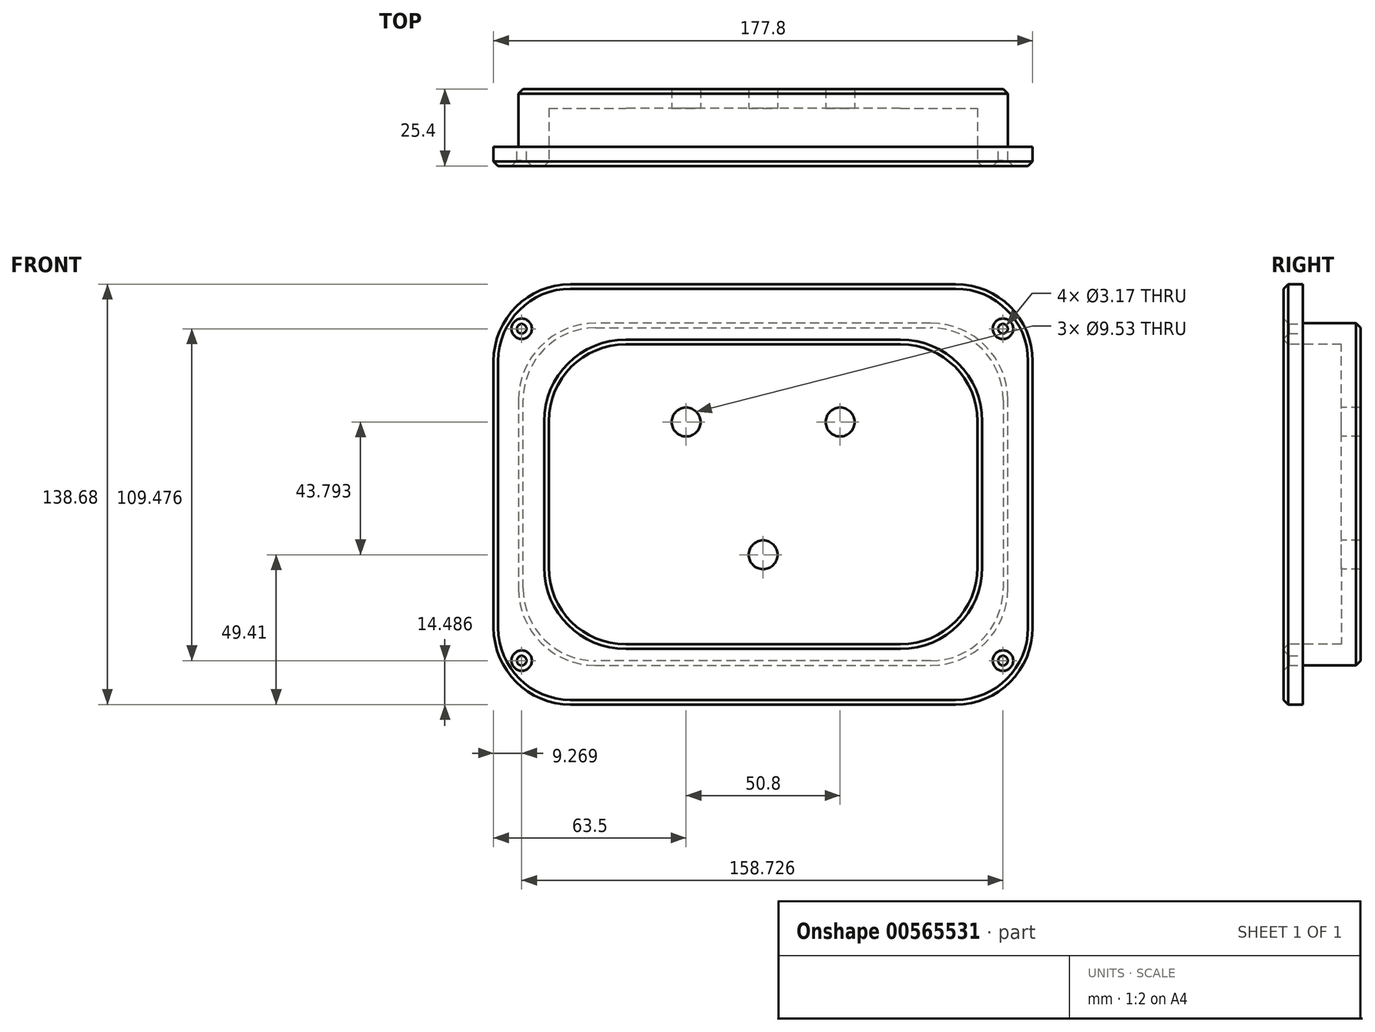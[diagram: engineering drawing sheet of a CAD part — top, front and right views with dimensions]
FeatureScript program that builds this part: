
annotation { "Feature Type Name" : "Feature", "Feature Type Description" : "" }
export const myFeature = defineFeature(function(context is Context, id is Id, definition is map)
    precondition{}
    {
        {
            var Q0;
            Q0=qCreatedBy(makeId("Front.planeOp"),FACE);
            var sketch = newSketch(context, id + "F0", { "sketchPlane" : qUnion([Q0])});
            skLineSegment(sketch, "E0.bottom", {"start": v(88.9, 69.34) * mm, "end": v(-88.9, 69.34) * mm});
            skLineSegment(sketch, "E0.top", {"start": v(88.9, -69.34) * mm, "end": v(-88.9, -69.34) * mm});
            skLineSegment(sketch, "E0.left", {"start": v(88.9, 69.34) * mm, "end": v(88.9, -69.34) * mm});
            skLineSegment(sketch, "E0.right", {"start": v(-88.9, 69.34) * mm, "end": v(-88.9, -69.34) * mm});
            skPoint(sketch, "E0.middle", {"position": v(0, 0) * mm});
            skSolve(sketch);
        }
        {
            var Q0;
            Q0=makeQuery(id+"F0.imprint","IMPRINT",FACE,{"disambiguationData":[TD([[makeQuery(id+"F0.imprint","IMPRINT",EDGE,{"derivedFrom":sQuery(id+"F0.wireOp",EDGE,"E0.bottom")}),1.0]])]});
            extrude(context, id + "F1", {"entities" : qUnion([Q0]), "depth" : 25.4 * mm, "offsetDistance" : 25.4 * mm});
        }
        {
            var Q0;
            Q0=makeQuery(id+"F1.opExtrude","CAP_FACE",FACE,{"disambiguationData":[OSD([sQuery(id+"F0.wireOp",EDGE,"E0.bottom"),sQuery(id+"F0.wireOp",EDGE,"E0.top"),sQuery(id+"F0.wireOp",EDGE,"E0.left"),sQuery(id+"F0.wireOp",EDGE,"E0.right")])],"isStart":true});
            var sketch = newSketch(context, id + "F2", { "sketchPlane" : qUnion([Q0])});
            skLineSegment(sketch, "E1.bottom", {"start": v(80.69, -56.44) * mm, "end": v(-80.69, -56.44) * mm});
            skLineSegment(sketch, "E1.top", {"start": v(80.69, 56.44) * mm, "end": v(-80.69, 56.44) * mm});
            skLineSegment(sketch, "E1.left", {"start": v(80.69, -56.44) * mm, "end": v(80.69, 56.44) * mm});
            skLineSegment(sketch, "E1.right", {"start": v(-80.69, -56.44) * mm, "end": v(-80.69, 56.44) * mm});
            skPoint(sketch, "E1.middle", {"position": v(0, 0) * mm});
            skSolve(sketch);
        }
        {
            var Q0;
            Q0=makeQuery(id+"F2.imprint","IMPRINT",FACE,{"disambiguationData":[TD([[makeQuery(id+"F2.imprint","IMPRINT",EDGE,{"derivedFrom":sQuery(id+"F2.wireOp",EDGE,"E1.bottom")}),1.0]])]});
            extrude(context, id + "F3", {"entities" : qUnion([Q0]), "operationType" : NewBodyOperationType.REMOVE, "oppositeDirection" : true, "depth" : 19.05 * mm, "offsetDistance" : 25.4 * mm});
        }
        {
            var Q0;
            Q0=makeQuery(id+"F1.opExtrude","CAP_FACE",FACE,{"disambiguationData":[OSD([sQuery(id+"F0.wireOp",EDGE,"E0.bottom"),sQuery(id+"F0.wireOp",EDGE,"E0.top"),sQuery(id+"F0.wireOp",EDGE,"E0.left"),sQuery(id+"F0.wireOp",EDGE,"E0.right")])],"isStart":false});
            var sketch = newSketch(context, id + "F4", { "sketchPlane" : qUnion([Q0])});
            skLineSegment(sketch, "E2.bottom", {"start": v(70.71, -49.5) * mm, "end": v(-70.71, -49.5) * mm});
            skLineSegment(sketch, "E2.top", {"start": v(70.71, 49.5) * mm, "end": v(-70.71, 49.5) * mm});
            skLineSegment(sketch, "E2.left", {"start": v(70.71, -49.5) * mm, "end": v(70.71, 49.5) * mm});
            skLineSegment(sketch, "E2.right", {"start": v(-70.71, -49.5) * mm, "end": v(-70.71, 49.5) * mm});
            skPoint(sketch, "E2.middle", {"position": v(0, 0) * mm});
            skSolve(sketch);
        }
        {
            var Q0;
            Q0=makeQuery(id+"F4.imprint","IMPRINT",FACE,{"disambiguationData":[TD([[makeQuery(id+"F4.imprint","IMPRINT",EDGE,{"derivedFrom":sQuery(id+"F4.wireOp",EDGE,"E2.bottom")}),-1.0]])]});
            extrude(context, id + "F5", {"entities" : qUnion([Q0]), "operationType" : NewBodyOperationType.REMOVE, "oppositeDirection" : true, "depth" : 19.05 * mm, "offsetDistance" : 25.4 * mm});
        }
        {
            var Q0;
            Q0=makeQuery(id+"F1.opExtrude","SWEPT_EDGE",EDGE,{"disambiguationData":[OSD([sQuery(id+"F0.wireOp",EDGE,"E0.bottom"),sQuery(id+"F0.wireOp",EDGE,"E0.left")])]});
            var Q1;
            Q1=makeQuery(id+"F1.opExtrude","SWEPT_EDGE",EDGE,{"disambiguationData":[OSD([sQuery(id+"F0.wireOp",EDGE,"E0.top"),sQuery(id+"F0.wireOp",EDGE,"E0.left")])]});
            var Q2;
            Q2=makeQuery(id+"F1.opExtrude","SWEPT_EDGE",EDGE,{"disambiguationData":[OSD([sQuery(id+"F0.wireOp",EDGE,"E0.top"),sQuery(id+"F0.wireOp",EDGE,"E0.right")])]});
            var Q3;
            Q3=makeQuery(id+"F1.opExtrude","SWEPT_EDGE",EDGE,{"disambiguationData":[OSD([sQuery(id+"F0.wireOp",EDGE,"E0.bottom"),sQuery(id+"F0.wireOp",EDGE,"E0.right")])]});
            var Q4;
            Q4=makeQuery(id+"F5.boolean.opBoolean","COPY",EDGE,{"derivedFrom":makeQuery(id+"F5.opExtrude","SWEPT_EDGE",EDGE,{"disambiguationData":[OSD([sQuery(id+"F4.wireOp",EDGE,"E2.top"),sQuery(id+"F4.wireOp",EDGE,"E2.right")])]})});
            var Q5;
            Q5=makeQuery(id+"F5.boolean.opBoolean","COPY",EDGE,{"derivedFrom":makeQuery(id+"F5.opExtrude","SWEPT_EDGE",EDGE,{"disambiguationData":[OSD([sQuery(id+"F4.wireOp",EDGE,"E2.top"),sQuery(id+"F4.wireOp",EDGE,"E2.left")])]})});
            var Q6;
            Q6=makeQuery(id+"F5.boolean.opBoolean","COPY",EDGE,{"derivedFrom":makeQuery(id+"F5.opExtrude","SWEPT_EDGE",EDGE,{"disambiguationData":[OSD([sQuery(id+"F4.wireOp",EDGE,"E2.bottom"),sQuery(id+"F4.wireOp",EDGE,"E2.left")])]})});
            var Q7;
            Q7=makeQuery(id+"F5.boolean.opBoolean","COPY",EDGE,{"derivedFrom":makeQuery(id+"F5.opExtrude","SWEPT_EDGE",EDGE,{"disambiguationData":[OSD([sQuery(id+"F4.wireOp",EDGE,"E2.bottom"),sQuery(id+"F4.wireOp",EDGE,"E2.right")])]})});
            var Q8;
            Q8=makeQuery(id+"F3.boolean.opBoolean","COPY",EDGE,{"derivedFrom":makeQuery(id+"F3.opExtrude","SWEPT_EDGE",EDGE,{"disambiguationData":[OSD([sQuery(id+"F2.wireOp",EDGE,"E1.bottom"),sQuery(id+"F2.wireOp",EDGE,"E1.right")])]})});
            var Q9;
            Q9=makeQuery(id+"F3.boolean.opBoolean","COPY",EDGE,{"derivedFrom":makeQuery(id+"F3.opExtrude","SWEPT_EDGE",EDGE,{"disambiguationData":[OSD([sQuery(id+"F2.wireOp",EDGE,"E1.top"),sQuery(id+"F2.wireOp",EDGE,"E1.right")])]})});
            var Q10;
            Q10=makeQuery(id+"F3.boolean.opBoolean","COPY",EDGE,{"derivedFrom":makeQuery(id+"F3.opExtrude","SWEPT_EDGE",EDGE,{"disambiguationData":[OSD([sQuery(id+"F2.wireOp",EDGE,"E1.bottom"),sQuery(id+"F2.wireOp",EDGE,"E1.left")])]})});
            var Q11;
            Q11=makeQuery(id+"F3.boolean.opBoolean","COPY",EDGE,{"derivedFrom":makeQuery(id+"F3.opExtrude","SWEPT_EDGE",EDGE,{"disambiguationData":[OSD([sQuery(id+"F2.wireOp",EDGE,"E1.top"),sQuery(id+"F2.wireOp",EDGE,"E1.left")])]})});
            fillet(context, id + "F6", {"entities" : qUnion([Q0, Q1, Q2, Q3, Q4, Q5, Q6, Q7, Q8, Q9, Q10, Q11]), "radius" : 25.4 * mm, "tangentPropagation" : true, "allowEdgeOverflow" : false});
        }
        {
            var Q0;
            Q0=makeQuery(id+"F5.boolean.opBoolean","COPY",FACE,{"derivedFrom":makeQuery(id+"F5.opExtrude","CAP_FACE",FACE,{"disambiguationData":[OSD([sQuery(id+"F4.wireOp",EDGE,"E2.bottom"),sQuery(id+"F4.wireOp",EDGE,"E2.top"),sQuery(id+"F4.wireOp",EDGE,"E2.left"),sQuery(id+"F4.wireOp",EDGE,"E2.right")])],"isStart":false})});
            var sketch = newSketch(context, id + "F7", { "sketchPlane" : qUnion([Q0])});
            skCircle(sketch, "E3", {"center": v(-25.4, 23.86) * mm, "radius": 4.76 * mm});
            skCircle(sketch, "E4", {"center": v(25.4, 23.86) * mm, "radius": 4.76 * mm});
            skLineSegment(sketch, "E5", {"start": v(0, 65.45) * mm, "end": v(0, -56.23) * mm, "construction": true});
            skCircle(sketch, "E6", {"center": v(0, -19.93) * mm, "radius": 4.76 * mm});
            skSolve(sketch);
        }
        {
            var Q0;
            Q0=makeQuery(id+"F7.imprint","IMPRINT",FACE,{"disambiguationData":[TD([[makeQuery(id+"F7.imprint","IMPRINT",EDGE,{"derivedFrom":sQuery(id+"F7.wireOp",EDGE,"E3")}),1.0]])]});
            var Q1;
            Q1=makeQuery(id+"F7.imprint","IMPRINT",FACE,{"disambiguationData":[TD([[makeQuery(id+"F7.imprint","IMPRINT",EDGE,{"derivedFrom":sQuery(id+"F7.wireOp",EDGE,"E4")}),1.0]])]});
            var Q2;
            Q2=makeQuery(id+"F7.imprint","IMPRINT",FACE,{"disambiguationData":[TD([[makeQuery(id+"F7.imprint","IMPRINT",EDGE,{"derivedFrom":sQuery(id+"F7.wireOp",EDGE,"E6")}),1.0]])]});
            extrude(context, id + "F8", {"entities" : qUnion([Q0, Q1, Q2]), "operationType" : NewBodyOperationType.REMOVE, "endBound" : BoundingType.THROUGH_ALL, "oppositeDirection" : true, "depth" : 25.4 * mm, "offsetDistance" : 25.4 * mm});
        }
        {
            var Q0;
            Q0=makeQuery(id+"F5.boolean.opBoolean","COPY",EDGE,{"derivedFrom":makeQuery(id+"F5.opExtrude","CAP_EDGE",EDGE,{"disambiguationData":[OSD([sQuery(id+"F4.wireOp",EDGE,"E2.bottom")])],"isStart":true})});
            var Q1;
            Q1=makeQuery(id+"F6.opFillet","BLEND_EDGE",EDGE,{"blendedFrom":[makeQuery(id+"F5.boolean.opBoolean","COPY",EDGE,{"derivedFrom":makeQuery(id+"F5.opExtrude","SWEPT_EDGE",EDGE,{"disambiguationData":[OSD([sQuery(id+"F4.wireOp",EDGE,"E2.bottom"),sQuery(id+"F4.wireOp",EDGE,"E2.left")])]})}),makeQuery(id+"F1.opExtrude","CAP_FACE",FACE,{"disambiguationData":[OSD([sQuery(id+"F0.wireOp",EDGE,"E0.bottom"),sQuery(id+"F0.wireOp",EDGE,"E0.top"),sQuery(id+"F0.wireOp",EDGE,"E0.left"),sQuery(id+"F0.wireOp",EDGE,"E0.right")])],"isStart":false})],"blendedInto":[makeQuery(id+"F1.opExtrude","CAP_FACE",FACE,{"disambiguationData":[OSD([sQuery(id+"F0.wireOp",EDGE,"E0.bottom"),sQuery(id+"F0.wireOp",EDGE,"E0.top"),sQuery(id+"F0.wireOp",EDGE,"E0.left"),sQuery(id+"F0.wireOp",EDGE,"E0.right")])],"isStart":false})]});
            var Q2;
            Q2=makeQuery(id+"F5.boolean.opBoolean","COPY",EDGE,{"derivedFrom":makeQuery(id+"F5.opExtrude","CAP_EDGE",EDGE,{"disambiguationData":[OSD([sQuery(id+"F4.wireOp",EDGE,"E2.left")])],"isStart":true})});
            var Q3;
            Q3=makeQuery(id+"F6.opFillet","BLEND_EDGE",EDGE,{"blendedFrom":[makeQuery(id+"F5.boolean.opBoolean","COPY",EDGE,{"derivedFrom":makeQuery(id+"F5.opExtrude","SWEPT_EDGE",EDGE,{"disambiguationData":[OSD([sQuery(id+"F4.wireOp",EDGE,"E2.top"),sQuery(id+"F4.wireOp",EDGE,"E2.left")])]})}),makeQuery(id+"F1.opExtrude","CAP_FACE",FACE,{"disambiguationData":[OSD([sQuery(id+"F0.wireOp",EDGE,"E0.bottom"),sQuery(id+"F0.wireOp",EDGE,"E0.top"),sQuery(id+"F0.wireOp",EDGE,"E0.left"),sQuery(id+"F0.wireOp",EDGE,"E0.right")])],"isStart":false})],"blendedInto":[makeQuery(id+"F1.opExtrude","CAP_FACE",FACE,{"disambiguationData":[OSD([sQuery(id+"F0.wireOp",EDGE,"E0.bottom"),sQuery(id+"F0.wireOp",EDGE,"E0.top"),sQuery(id+"F0.wireOp",EDGE,"E0.left"),sQuery(id+"F0.wireOp",EDGE,"E0.right")])],"isStart":false})]});
            var Q4;
            Q4=makeQuery(id+"F1.opExtrude","CAP_EDGE",EDGE,{"disambiguationData":[OSD([sQuery(id+"F0.wireOp",EDGE,"E0.right")])],"isStart":false});
            var Q5;
            {var subQ0=sQuery(id+"F0.wireOp",EDGE,"E0.right");var subQ1=sQuery(id+"F0.wireOp",EDGE,"E0.top");Q5=makeQuery(id+"F6.opFillet","BLEND_EDGE",EDGE,{"blendedFrom":[makeQuery(id+"F1.opExtrude","SWEPT_EDGE",EDGE,{"disambiguationData":[OSD([subQ1,subQ0])]}),makeQuery(id+"F1.opExtrude","CAP_FACE",FACE,{"disambiguationData":[OSD([sQuery(id+"F0.wireOp",EDGE,"E0.bottom"),subQ1,sQuery(id+"F0.wireOp",EDGE,"E0.left"),subQ0])],"isStart":false})],"blendedInto":[makeQuery(id+"F1.opExtrude","CAP_FACE",FACE,{"disambiguationData":[OSD([sQuery(id+"F0.wireOp",EDGE,"E0.bottom"),subQ1,sQuery(id+"F0.wireOp",EDGE,"E0.left"),subQ0])],"isStart":false})]});}
            var Q6;
            Q6=makeQuery(id+"F6.opFillet","BLEND_EDGE",EDGE,{"blendedFrom":[makeQuery(id+"F3.boolean.opBoolean","COPY",EDGE,{"derivedFrom":makeQuery(id+"F3.opExtrude","SWEPT_EDGE",EDGE,{"disambiguationData":[OSD([sQuery(id+"F2.wireOp",EDGE,"E1.bottom"),sQuery(id+"F2.wireOp",EDGE,"E1.left")])]})}),makeQuery(id+"F1.opExtrude","CAP_FACE",FACE,{"disambiguationData":[OSD([sQuery(id+"F0.wireOp",EDGE,"E0.bottom"),sQuery(id+"F0.wireOp",EDGE,"E0.top"),sQuery(id+"F0.wireOp",EDGE,"E0.left"),sQuery(id+"F0.wireOp",EDGE,"E0.right")])],"isStart":true})],"blendedInto":[makeQuery(id+"F1.opExtrude","CAP_FACE",FACE,{"disambiguationData":[OSD([sQuery(id+"F0.wireOp",EDGE,"E0.bottom"),sQuery(id+"F0.wireOp",EDGE,"E0.top"),sQuery(id+"F0.wireOp",EDGE,"E0.left"),sQuery(id+"F0.wireOp",EDGE,"E0.right")])],"isStart":true})]});
            var Q7;
            Q7=makeQuery(id+"F3.boolean.opBoolean","COPY",EDGE,{"derivedFrom":makeQuery(id+"F3.opExtrude","CAP_EDGE",EDGE,{"disambiguationData":[OSD([sQuery(id+"F2.wireOp",EDGE,"E1.bottom")])],"isStart":true})});
            chamfer(context, id + "F9", {"entities" : qUnion([Q0, Q1, Q2, Q3, Q4, Q5, Q6, Q7]), "width" : 1.52 * mm, "tangentPropagation" : true});
        }
        {
            var Q0;
            Q0=makeQuery(id+"F3.boolean.opBoolean","COPY",FACE,{"derivedFrom":makeQuery(id+"F3.opExtrude","CAP_FACE",FACE,{"disambiguationData":[OSD([sQuery(id+"F0.wireOp",EDGE,"E0.bottom"),sQuery(id+"F0.wireOp",EDGE,"E0.top"),sQuery(id+"F0.wireOp",EDGE,"E0.left"),sQuery(id+"F0.wireOp",EDGE,"E0.right"),sQuery(id+"F2.wireOp",EDGE,"E1.bottom"),sQuery(id+"F2.wireOp",EDGE,"E1.top"),sQuery(id+"F2.wireOp",EDGE,"E1.left"),sQuery(id+"F2.wireOp",EDGE,"E1.right")])],"isStart":false})});
            var sketch = newSketch(context, id + "F10", { "sketchPlane" : qUnion([Q0])});
            skCircle(sketch, "E7", {"center": v(-79.1, 54.62) * mm, "radius": 1.59 * mm});
            skCircle(sketch, "E8", {"center": v(79.63, 54.62) * mm, "radius": 1.59 * mm});
            skCircle(sketch, "E9", {"center": v(79.63, -54.85) * mm, "radius": 1.59 * mm});
            skCircle(sketch, "E10", {"center": v(-79.1, -54.85) * mm, "radius": 1.59 * mm});
            skSolve(sketch);
        }
        {
            var Q0;
            Q0=makeQuery(id+"F10.imprint","IMPRINT",FACE,{"disambiguationData":[TD([[makeQuery(id+"F10.imprint","IMPRINT",EDGE,{"derivedFrom":sQuery(id+"F10.wireOp",EDGE,"E7")}),1.0]])]});
            var Q1;
            Q1=makeQuery(id+"F10.imprint","IMPRINT",FACE,{"disambiguationData":[TD([[makeQuery(id+"F10.imprint","IMPRINT",EDGE,{"derivedFrom":sQuery(id+"F10.wireOp",EDGE,"E8")}),1.0]])]});
            var Q2;
            Q2=makeQuery(id+"F10.imprint","IMPRINT",FACE,{"disambiguationData":[TD([[makeQuery(id+"F10.imprint","IMPRINT",EDGE,{"derivedFrom":sQuery(id+"F10.wireOp",EDGE,"E9")}),1.0]])]});
            var Q3;
            Q3=makeQuery(id+"F10.imprint","IMPRINT",FACE,{"disambiguationData":[TD([[makeQuery(id+"F10.imprint","IMPRINT",EDGE,{"derivedFrom":sQuery(id+"F10.wireOp",EDGE,"E10")}),1.0]])]});
            extrude(context, id + "F11", {"entities" : qUnion([Q0, Q1, Q2, Q3]), "operationType" : NewBodyOperationType.REMOVE, "endBound" : BoundingType.THROUGH_ALL, "oppositeDirection" : true, "depth" : 25.4 * mm, "offsetDistance" : 25.4 * mm});
        }
        {
            var Q0;
            Q0=makeQuery(id+"F11.boolean.opBoolean","INTERSECT",EDGE,{"derivedFrom":[makeQuery(id+"F1.opExtrude","CAP_FACE",FACE,{"disambiguationData":[OSD([sQuery(id+"F0.wireOp",EDGE,"E0.bottom"),sQuery(id+"F0.wireOp",EDGE,"E0.top"),sQuery(id+"F0.wireOp",EDGE,"E0.left"),sQuery(id+"F0.wireOp",EDGE,"E0.right")])],"isStart":false}),makeQuery(id+"F11.opExtrude","SWEPT_FACE",FACE,{"disambiguationData":[OSD([sQuery(id+"F10.wireOp",EDGE,"E8")])]})]});
            var Q1;
            Q1=makeQuery(id+"F11.boolean.opBoolean","INTERSECT",EDGE,{"derivedFrom":[makeQuery(id+"F1.opExtrude","CAP_FACE",FACE,{"disambiguationData":[OSD([sQuery(id+"F0.wireOp",EDGE,"E0.bottom"),sQuery(id+"F0.wireOp",EDGE,"E0.top"),sQuery(id+"F0.wireOp",EDGE,"E0.left"),sQuery(id+"F0.wireOp",EDGE,"E0.right")])],"isStart":false}),makeQuery(id+"F11.opExtrude","SWEPT_FACE",FACE,{"disambiguationData":[OSD([sQuery(id+"F10.wireOp",EDGE,"E7")])]})]});
            var Q2;
            Q2=makeQuery(id+"F11.boolean.opBoolean","INTERSECT",EDGE,{"derivedFrom":[makeQuery(id+"F1.opExtrude","CAP_FACE",FACE,{"disambiguationData":[OSD([sQuery(id+"F0.wireOp",EDGE,"E0.bottom"),sQuery(id+"F0.wireOp",EDGE,"E0.top"),sQuery(id+"F0.wireOp",EDGE,"E0.left"),sQuery(id+"F0.wireOp",EDGE,"E0.right")])],"isStart":false}),makeQuery(id+"F11.opExtrude","SWEPT_FACE",FACE,{"disambiguationData":[OSD([sQuery(id+"F10.wireOp",EDGE,"E10")])]})]});
            var Q3;
            Q3=makeQuery(id+"F11.boolean.opBoolean","INTERSECT",EDGE,{"derivedFrom":[makeQuery(id+"F1.opExtrude","CAP_FACE",FACE,{"disambiguationData":[OSD([sQuery(id+"F0.wireOp",EDGE,"E0.bottom"),sQuery(id+"F0.wireOp",EDGE,"E0.top"),sQuery(id+"F0.wireOp",EDGE,"E0.left"),sQuery(id+"F0.wireOp",EDGE,"E0.right")])],"isStart":false}),makeQuery(id+"F11.opExtrude","SWEPT_FACE",FACE,{"disambiguationData":[OSD([sQuery(id+"F10.wireOp",EDGE,"E9")])]})]});
            chamfer(context, id + "F12", {"entities" : qUnion([Q0, Q1, Q2, Q3]), "width" : 1.78 * mm, "tangentPropagation" : true});
        }
    });
